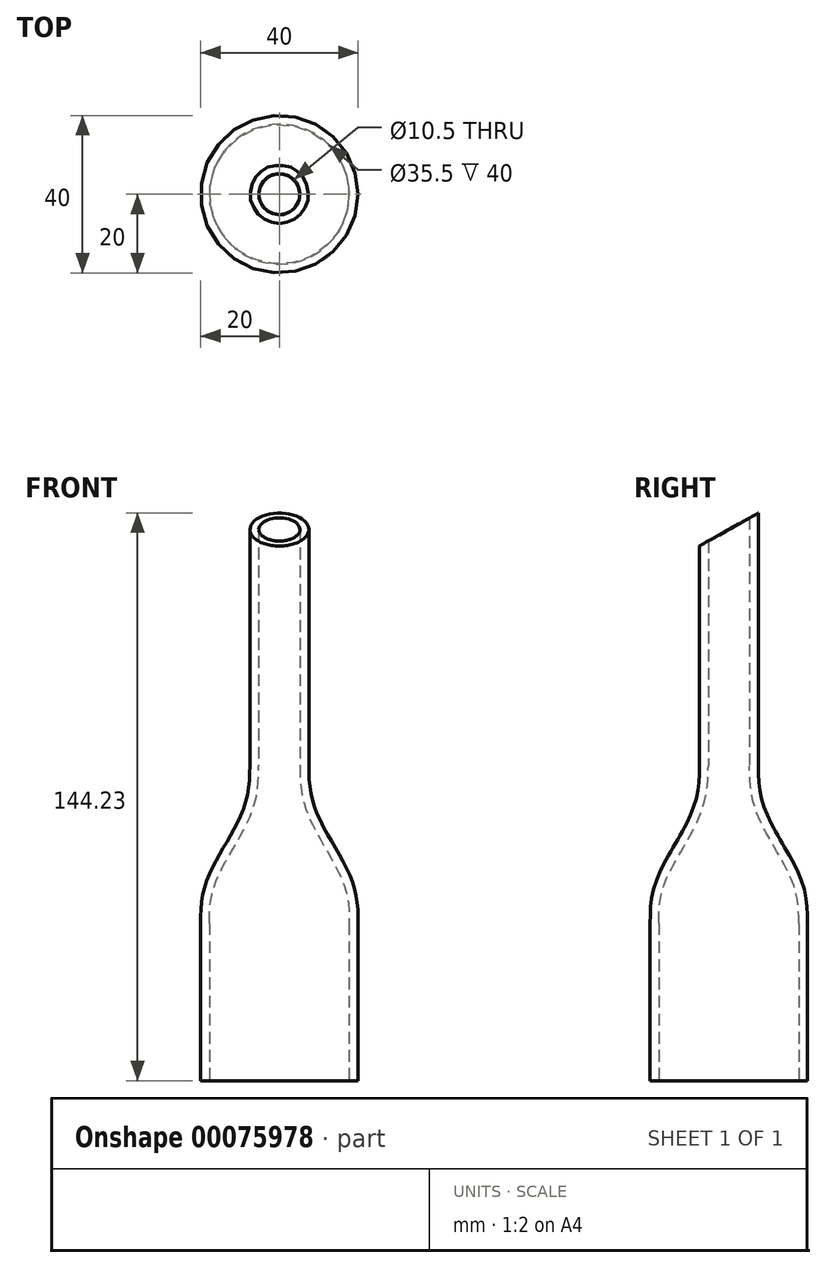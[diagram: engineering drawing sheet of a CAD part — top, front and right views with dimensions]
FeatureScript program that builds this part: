
annotation { "Feature Type Name" : "Feature", "Feature Type Description" : "" }
export const myFeature = defineFeature(function(context is Context, id is Id, definition is map)
    precondition{}
    {
        {
            var Q0;
            Q0=qCreatedBy(makeId("Top.planeOp"),FACE);
            var sketch = newSketch(context, id + "F0", { "sketchPlane" : qUnion([Q0])});
            skCircle(sketch, "E0", {"center": v(0, 0) * mm, "radius": 20 * mm});
            skSolve(sketch);
        }
        {
            var Q0;
            Q0=makeQuery(id+"F0.imprint","IMPRINT",FACE,{"disambiguationData":[TD([[makeQuery(id+"F0.imprint","IMPRINT",EDGE,{"derivedFrom":sQuery(id+"F0.wireOp",EDGE,"97585958-37b8-45a1-9a76-0f9e5c963641")}),-1.0]])]});
            var Q1;
            Q1=makeQuery(id+"F0.imprint","IMPRINT",FACE,{"disambiguationData":[TD([[makeQuery(id+"F0.imprint","IMPRINT",EDGE,{"derivedFrom":sQuery(id+"F0.wireOp",EDGE,"E0")}),1.0]])]});
            extrude(context, id + "F1", {"entities" : qUnion([Q0, Q1]), "depth" : 40 * mm});
        }
        {
            var Q0;
            Q0=qCreatedBy(makeId("Top.planeOp"),FACE);
            cPlane(context, id + "F2", {"entities" : qUnion([Q0]), "cplaneType" : CPlaneType.OFFSET, "offset" : 80 * mm, "width" : 150 * mm, "height" : 150 * mm});
        }
        {
            var Q0;
            Q0=qCreatedBy(id+"F2.planeOp",FACE);
            var sketch = newSketch(context, id + "F3", { "sketchPlane" : qUnion([Q0])});
            skCircle(sketch, "E1", {"center": v(0, 0) * mm, "radius": 7.5 * mm});
            skSolve(sketch);
        }
        {
            var Q0;
            Q0=makeQuery(id+"F3.imprint","IMPRINT",FACE,{"disambiguationData":[TD([[makeQuery(id+"F3.imprint","IMPRINT",EDGE,{"derivedFrom":sQuery(id+"F3.wireOp",EDGE,"E1")}),1.0]])]});
            extrude(context, id + "F4", {"entities" : qUnion([Q0]), "depth" : 80 * mm});
        }
        {
            var Q0;
            Q0=makeQuery(id+"F4.opExtrude","CAP_FACE",FACE,{"disambiguationData":[OSD([sQuery(id+"F3.wireOp",EDGE,"E1")])],"isStart":true});
            var Q1;
            Q1=makeQuery(id+"F1.opExtrude","CAP_FACE",FACE,{"disambiguationData":[OSD([sQuery(id+"F0.wireOp",EDGE,"E0")])],"isStart":false});
            loft(context, id + "F5", {"operationType" : NewBodyOperationType.ADD, "startCondition" : LoftEndDerivativeType.MATCH_CURVATURE, "startMagnitude" : 1, "endCondition" : LoftEndDerivativeType.MATCH_CURVATURE, "endMagnitude" : 1, "sheetProfilesArray" : [{ "sheetProfileEntities" : qUnion([Q0]) }, { "sheetProfileEntities" : qUnion([Q1]) }]});
        }
        {
            var Q0;
            Q0=makeQuery(id+"F4.opExtrude","CAP_FACE",FACE,{"disambiguationData":[OSD([sQuery(id+"F3.wireOp",EDGE,"E1")])],"isStart":false});
            var Q1;
            Q1=makeQuery(id+"F1.opExtrude","CAP_FACE",FACE,{"disambiguationData":[OSD([sQuery(id+"F0.wireOp",EDGE,"E0")])],"isStart":true});
            shell(context, id + "F6", {"entities" : qUnion([Q0, Q1]), "thickness" : 2.25 * mm});
        }
        {
            var Q0;
            Q0=qCreatedBy(makeId("Right.planeOp"),FACE);
            var sketch = newSketch(context, id + "F7", { "sketchPlane" : qUnion([Q0])});
            skLineSegment(sketch, "E2", {"start": v(-15.86, 131.18) * mm, "end": v(16.1, 149.03) * mm});
            skLineSegment(sketch, "E3", {"start": v(16.1, 149.03) * mm, "end": v(16.1, 165.1) * mm});
            skLineSegment(sketch, "E4", {"start": v(16.1, 165.1) * mm, "end": v(-17.98, 168.28) * mm});
            skLineSegment(sketch, "E5", {"start": v(-17.98, 168.28) * mm, "end": v(-15.86, 131.18) * mm});
            skSolve(sketch);
        }
        {
            var Q0;
            Q0=makeQuery(id+"F7.imprint","IMPRINT",FACE,{"disambiguationData":[TD([[makeQuery(id+"F7.imprint","IMPRINT",EDGE,{"derivedFrom":sQuery(id+"F7.wireOp",EDGE,"E2")}),1.0]])]});
            extrude(context, id + "F8", {"entities" : qUnion([Q0]), "operationType" : NewBodyOperationType.REMOVE, "depth" : 25 * mm, "hasSecondDirection" : true, "secondDirectionOppositeDirection" : true, "secondDirectionDepth" : 25 * mm});
        }
    });
